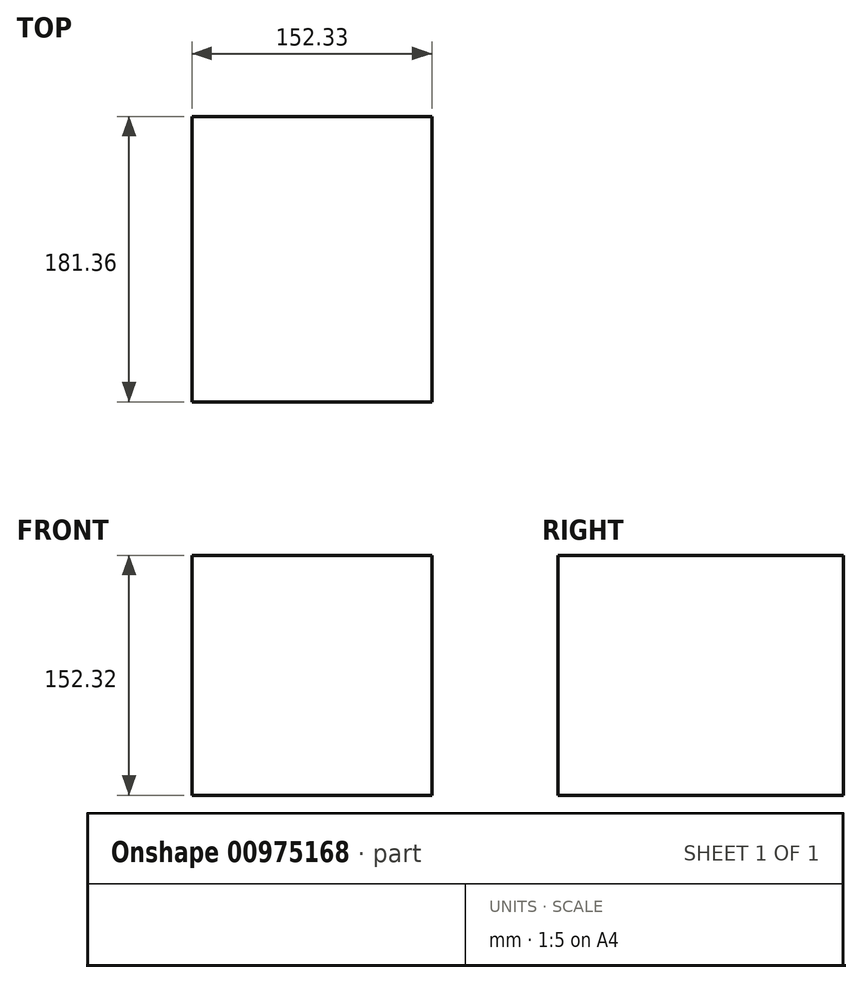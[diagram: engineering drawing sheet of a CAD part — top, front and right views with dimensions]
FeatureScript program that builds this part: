
annotation { "Feature Type Name" : "Feature", "Feature Type Description" : "" }
export const myFeature = defineFeature(function(context is Context, id is Id, definition is map)
    precondition{}
    {
        {
            var Q0;
            Q0=qCreatedBy(makeId("Front.planeOp"),FACE);
            var sketch = newSketch(context, id + "F0", { "sketchPlane" : qUnion([Q0])});
            skLineSegment(sketch, "E0", {"start": v(-76.17, 75.9) * mm, "end": v(76.14, 75.9) * mm});
            skLineSegment(sketch, "E1", {"start": v(76.14, 75.9) * mm, "end": v(76.14, -76.43) * mm});
            skLineSegment(sketch, "E2", {"start": v(76.14, -76.43) * mm, "end": v(-76.2, -76.43) * mm});
            skLineSegment(sketch, "E3", {"start": v(-76.2, -76.43) * mm, "end": v(-76.17, 75.9) * mm});
            skSolve(sketch);
        }
        {
            var Q0;
            Q0=makeQuery(id+"F0.imprint","IMPRINT",FACE,{"disambiguationData":[TD([[makeQuery(id+"F0.imprint","IMPRINT",EDGE,{"derivedFrom":sQuery(id+"F0.wireOp",EDGE,"E0")}),-1.0]])]});
            extrude(context, id + "F1", {"entities" : qUnion([Q0]), "oppositeDirection" : true, "depth" : 75.4 * mm, "offsetDistance" : 25.4 * mm});
        }
        {
            var Q0;
            Q0=makeQuery(id+"F1.opExtrude","CAP_FACE",FACE,{"disambiguationData":[OSD([sQuery(id+"F0.wireOp",EDGE,"E0"),sQuery(id+"F0.wireOp",EDGE,"E1"),sQuery(id+"F0.wireOp",EDGE,"E2"),sQuery(id+"F0.wireOp",EDGE,"E3")])],"isStart":false});
            var Q1;
            Q1=makeQuery(id+"F1.opExtrude","CAP_FACE",FACE,{"disambiguationData":[OSD([sQuery(id+"F0.wireOp",EDGE,"E0"),sQuery(id+"F0.wireOp",EDGE,"E1"),sQuery(id+"F0.wireOp",EDGE,"E2"),sQuery(id+"F0.wireOp",EDGE,"E3")])],"isStart":true});
            extrude(context, id + "F2", {"entities" : qUnion([Q0, Q1]), "operationType" : NewBodyOperationType.ADD, "depth" : 4.94 * mm, "offsetDistance" : 25.4 * mm});
        }
        {
            var Q0;
            Q0=makeQuery(id+"F1.opExtrude","CAP_FACE",FACE,{"disambiguationData":[OSD([sQuery(id+"F0.wireOp",EDGE,"E0"),sQuery(id+"F0.wireOp",EDGE,"E1"),sQuery(id+"F0.wireOp",EDGE,"E2"),sQuery(id+"F0.wireOp",EDGE,"E3")])],"isStart":true});
            extrude(context, id + "F3", {"entities" : qUnion([Q0]), "operationType" : NewBodyOperationType.ADD, "depth" : 75.6 * mm, "offsetDistance" : 25.4 * mm});
        }
        {
            var Q0;
            {var subQ0=sQuery(id+"F0.wireOp",EDGE,"E3");var subQ1=sQuery(id+"F0.wireOp",EDGE,"E2");var subQ2=sQuery(id+"F0.wireOp",EDGE,"E1");var subQ3=sQuery(id+"F0.wireOp",EDGE,"E0");Q0=makeQuery(id+"F2.opExtrude","CAP_FACE",FACE,{"disambiguationData":[OSD([subQ3,subQ2,subQ1,subQ0]),TDD([makeQuery(id+"F1.opExtrude","CAP_FACE",FACE,{"disambiguationData":[OSD([subQ3,subQ2,subQ1,subQ0])],"isStart":false})])],"isStart":false});}
            extrude(context, id + "F4", {"entities" : qUnion([Q0]), "operationType" : NewBodyOperationType.ADD, "depth" : 25.4 * mm, "offsetDistance" : 25.4 * mm});
        }
    });
